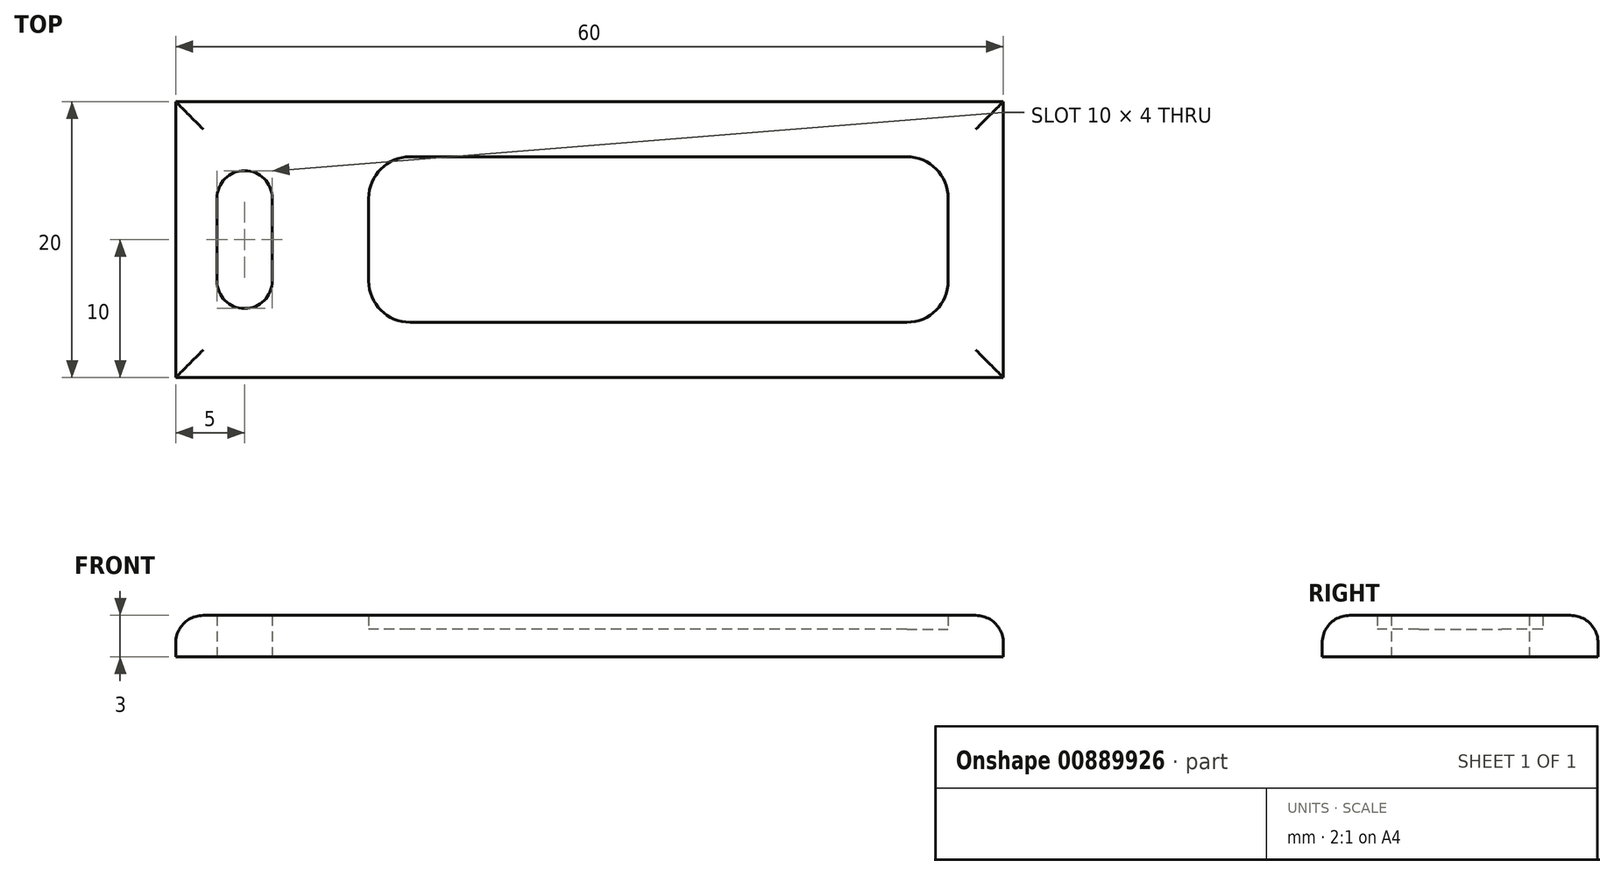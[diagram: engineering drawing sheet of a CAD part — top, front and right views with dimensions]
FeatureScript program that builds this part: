
annotation { "Feature Type Name" : "Feature", "Feature Type Description" : "" }
export const myFeature = defineFeature(function(context is Context, id is Id, definition is map)
    precondition{}
    {
        {
            var Q0;
            Q0=qCreatedBy(makeId("Top.planeOp"),FACE);
            var sketch = newSketch(context, id + "F0", { "sketchPlane" : qUnion([Q0])});
            skLineSegment(sketch, "E0.bottom", {"start": v(25, -10) * mm, "end": v(-25, -10) * mm});
            skLineSegment(sketch, "E0.top", {"start": v(25, 10) * mm, "end": v(-25, 10) * mm});
            skLineSegment(sketch, "E0.left", {"start": v(25, -10) * mm, "end": v(25, 10) * mm});
            skLineSegment(sketch, "E0.right", {"start": v(-25, -10) * mm, "end": v(-25, 10) * mm});
            skPoint(sketch, "E0.middle", {"position": v(0, 0) * mm});
            skLineSegment(sketch, "E1.bottom", {"start": v(-25, 10) * mm, "end": v(-35, 10) * mm});
            skLineSegment(sketch, "E1.top", {"start": v(-25, -10) * mm, "end": v(-35, -10) * mm});
            skLineSegment(sketch, "E1.left", {"start": v(-25, 10) * mm, "end": v(-25, -10) * mm});
            skLineSegment(sketch, "E1.right", {"start": v(-35, 10) * mm, "end": v(-35, -10) * mm});
            skPoint(sketch, "E1.middle", {"position": v(-30, 0) * mm});
            skLineSegment(sketch, "E2.bottom", {"start": v(-30, 5) * mm, "end": v(-30, 5) * mm});
            skLineSegment(sketch, "E2.top", {"start": v(-30, -5) * mm, "end": v(-30, -5) * mm});
            skLineSegment(sketch, "E2.left", {"start": v(-28, 3) * mm, "end": v(-28, -3) * mm});
            skLineSegment(sketch, "E2.right", {"start": v(-32, 3) * mm, "end": v(-32, -3) * mm});
            skPoint(sketch, "E3.visualSharp", {"position": v(-28, 5) * mm});
            skArc(sketch, "E3.filletArc", {"start": v(-28, 3) * mm, "mid": v(-28.59, 4.41) * mm, "end": v(-30, 5) * mm});
            skPoint(sketch, "E4.visualSharp", {"position": v(-28, -5) * mm});
            skArc(sketch, "E4.filletArc", {"start": v(-30, -5) * mm, "mid": v(-28.59, -4.41) * mm, "end": v(-28, -3) * mm});
            skPoint(sketch, "E5.visualSharp", {"position": v(-32, -5) * mm});
            skArc(sketch, "E5.filletArc", {"start": v(-32, -3) * mm, "mid": v(-31.41, -4.41) * mm, "end": v(-30, -5) * mm});
            skPoint(sketch, "E6.visualSharp", {"position": v(-32, 5) * mm});
            skArc(sketch, "E6.filletArc", {"start": v(-30, 5) * mm, "mid": v(-31.41, 4.41) * mm, "end": v(-32, 3) * mm});
            skSolve(sketch);
        }
        {
            var Q0;
            Q0 = qSketchRegion(id + "F0", true);
            extrude(context, id + "F1", {"entities" : qUnion([Q0]), "depth" : 3 * mm, "offsetDistance" : 25 * mm});
        }
        {
            var Q0;
            Q0=qCreatedBy(makeId("Top.planeOp"),FACE);
            var sketch = newSketch(context, id + "F2", { "sketchPlane" : qUnion([Q0])});
            skLineSegment(sketch, "E7.bottom", {"start": v(18, -6) * mm, "end": v(-18, -6) * mm});
            skLineSegment(sketch, "E7.top", {"start": v(18, 6) * mm, "end": v(-18, 6) * mm});
            skLineSegment(sketch, "E7.left", {"start": v(21, -3) * mm, "end": v(21, 3) * mm});
            skLineSegment(sketch, "E7.right", {"start": v(-21, -3) * mm, "end": v(-21, 3) * mm});
            skPoint(sketch, "E7.middle", {"position": v(0, 0) * mm});
            skPoint(sketch, "E8.visualSharp", {"position": v(-21, 6) * mm});
            skArc(sketch, "E8.filletArc", {"start": v(-18, 6) * mm, "mid": v(-20.12, 5.12) * mm, "end": v(-21, 3) * mm});
            skPoint(sketch, "E9.visualSharp", {"position": v(21, 6) * mm});
            skArc(sketch, "E9.filletArc", {"start": v(21, 3) * mm, "mid": v(20.12, 5.12) * mm, "end": v(18, 6) * mm});
            skPoint(sketch, "E10.visualSharp", {"position": v(-21, -6) * mm});
            skArc(sketch, "E10.filletArc", {"start": v(-21, -3) * mm, "mid": v(-20.12, -5.12) * mm, "end": v(-18, -6) * mm});
            skPoint(sketch, "E11.visualSharp", {"position": v(21, -6) * mm});
            skArc(sketch, "E11.filletArc", {"start": v(18, -6) * mm, "mid": v(20.12, -5.12) * mm, "end": v(21, -3) * mm});
            skSolve(sketch);
        }
        {
            var Q0;
            Q0 = qSketchRegion(id + "F2", true);
            extrude(context, id + "F3", {"entities" : qUnion([Q0]), "depth" : 3 * mm, "offsetDistance" : 25 * mm});
        }
        {
            var Q0;
            Q0=makeQuery(id+"F3.opExtrude","SWEPT_BODY",BODY,{"disambiguationData":[OSD([sQuery(id+"F2.wireOp",EDGE,"E7.bottom"),sQuery(id+"F2.wireOp",EDGE,"E7.top"),sQuery(id+"F2.wireOp",EDGE,"E7.left"),sQuery(id+"F2.wireOp",EDGE,"E7.right"),sQuery(id+"F2.wireOp",EDGE,"E8.filletArc"),sQuery(id+"F2.wireOp",EDGE,"E9.filletArc"),sQuery(id+"F2.wireOp",EDGE,"E10.filletArc"),sQuery(id+"F2.wireOp",EDGE,"E11.filletArc")])]});
            transform(context, id + "F4", {"entities" : qUnion([Q0]), "transformType" : TransformType.TRANSLATION_3D, "dx" : 0 * mm, "dy" : 0 * mm, "dz" : 2 * mm, "makeCopy" : false});
        }
        {
            var Q0;
            Q0=makeQuery(id+"F3.opExtrude","SWEPT_BODY",BODY,{"disambiguationData":[OSD([sQuery(id+"F2.wireOp",EDGE,"E7.bottom"),sQuery(id+"F2.wireOp",EDGE,"E7.top"),sQuery(id+"F2.wireOp",EDGE,"E7.left"),sQuery(id+"F2.wireOp",EDGE,"E7.right"),sQuery(id+"F2.wireOp",EDGE,"E8.filletArc"),sQuery(id+"F2.wireOp",EDGE,"E9.filletArc"),sQuery(id+"F2.wireOp",EDGE,"E10.filletArc"),sQuery(id+"F2.wireOp",EDGE,"E11.filletArc")])]});
            var Q1;
            Q1=makeQuery(id+"F1.opExtrude","SWEPT_BODY",BODY,{"disambiguationData":[OSD([sQuery(id+"F0.wireOp",EDGE,"E0.bottom"),sQuery(id+"F0.wireOp",EDGE,"E0.top"),sQuery(id+"F0.wireOp",EDGE,"E0.left"),sQuery(id+"F0.wireOp",EDGE,"E1.bottom"),sQuery(id+"F0.wireOp",EDGE,"E1.top"),sQuery(id+"F0.wireOp",EDGE,"E1.right"),sQuery(id+"F0.wireOp",EDGE,"E2.left"),sQuery(id+"F0.wireOp",EDGE,"E2.right"),sQuery(id+"F0.wireOp",EDGE,"E3.filletArc"),sQuery(id+"F0.wireOp",EDGE,"E4.filletArc"),sQuery(id+"F0.wireOp",EDGE,"E5.filletArc"),sQuery(id+"F0.wireOp",EDGE,"E6.filletArc")])]});
            booleanBodies(context, id + "F5", {"operationType" : BooleanOperationType.SUBTRACTION, "tools" : qUnion([Q0]), "targets" : qUnion([Q1])});
        }
        {
            var Q0;
            Q0=makeQuery(id+"F1.opExtrude","CAP_EDGE",EDGE,{"disambiguationData":[OSD([sQuery(id+"F0.wireOp",EDGE,"E1.right")])],"isStart":false});
            var Q1;
            Q1=makeQuery(id+"F1.opExtrude","CAP_EDGE",EDGE,{"disambiguationData":[OSD([sQuery(id+"F0.wireOp",EDGE,"E0.left")])],"isStart":false});
            var Q2;
            Q2=makeQuery(id+"F1.opExtrude","CAP_EDGE",EDGE,{"disambiguationData":[OSD([sQuery(id+"F0.wireOp",EDGE,"E0.top"),sQuery(id+"F0.wireOp",EDGE,"E1.bottom")])],"isStart":false});
            var Q3;
            Q3=makeQuery(id+"F1.opExtrude","CAP_EDGE",EDGE,{"disambiguationData":[OSD([sQuery(id+"F0.wireOp",EDGE,"E0.bottom"),sQuery(id+"F0.wireOp",EDGE,"E1.top")])],"isStart":false});
            fillet(context, id + "F6", {"entities" : qUnion([Q0, Q1, Q2, Q3]), "radius" : 2 * mm, "tangentPropagation" : true, "allowEdgeOverflow" : false});
        }
    });
